# Revit family: PRD_FrankeWS_WCSqttngPns_CAMPUSConnectionSetSquatToilet_ZCMPX0007
name_source: partatom
category: Specialty Equipment
revit_build: Autodesk Revit 2018 (Build: 20190510_1515(x64)
units: mm (PartAtom-declared; Revit-internal decimal feet)

## family parameters
Always vertical = No
Cut with Voids When Loaded = No
OmniClass Number = 23.45.55.11
OmniClass Title = Sanitary Components
Part Type = Normal
Room Calculation Point = No
Round Connector Dimension = Use Diameter
Shared = No
Work Plane-Based = Yes

## types (1)
- ZCMPX0007
    AssetType = Fixed
    BIMObjectName = PRD_AR_WCSquattingPans_CAMPUSConnectionSetSquatToilet_ZCMPX0007
    BodyMaterial = PRD_AR_Brass
    Category = Pr_40_20_93_96, WC squatting pans
    Default Elevation = 1219 mm
    Description = Connection kit for squat pan, consisting of male connector and adapter, diameter 28mm, for flush valve.
    DurationUnit = year
    Features = male connector and adapter, diameter 28mm, for flush valve
    GrossWeight = 0.64 kg
    IfcExportAs = IfcSanitaryTerminalType
    IfcExportType = USERDEFINED
    Manufacturer = KWC Group AG
    ManufacturerName = KWC Group AG
    ManufacturerURL = www.kwc.com
    Material = Brass
    Model = ZCMPX0007
    ModelNumber = 2030027502
    ModelReference = ZCMPX0007
    Name = CAMPUS Connection set, squat toilet ZCMPX0007
    NetWeight = 0.61 kg
    NominalDepth = 0 mm  [stored 0 ft]
    NominalHeight = 0 mm  [stored 0 ft]
    NominalLength = 0 mm  [stored 0 ft]
    NominalWidth = 0 mm  [stored 0 ft]
    ProductCode = 205.0638.903
    ProductInformation = https://pim.kwc.com
    Quantity = 1
    QuantityUom = Piece
    Status = New
    TailorMade = No
    URL = www.kwc.com
    Uniclass2015Code = Pr_40_20_93_96
    Uniclass2015Title = WC squatting pans
    Uniclass2015Version = Products v1.23
    Version = 1
    WarrantyDurationUnit = year

note: [stored X ft] marks values corroborated as IEEE doubles in the binary element streams (Revit-internal decimal feet)

## geometry (parser evidence)
native form markers: Sweep x3
no freeform markers — native parametric forms only
